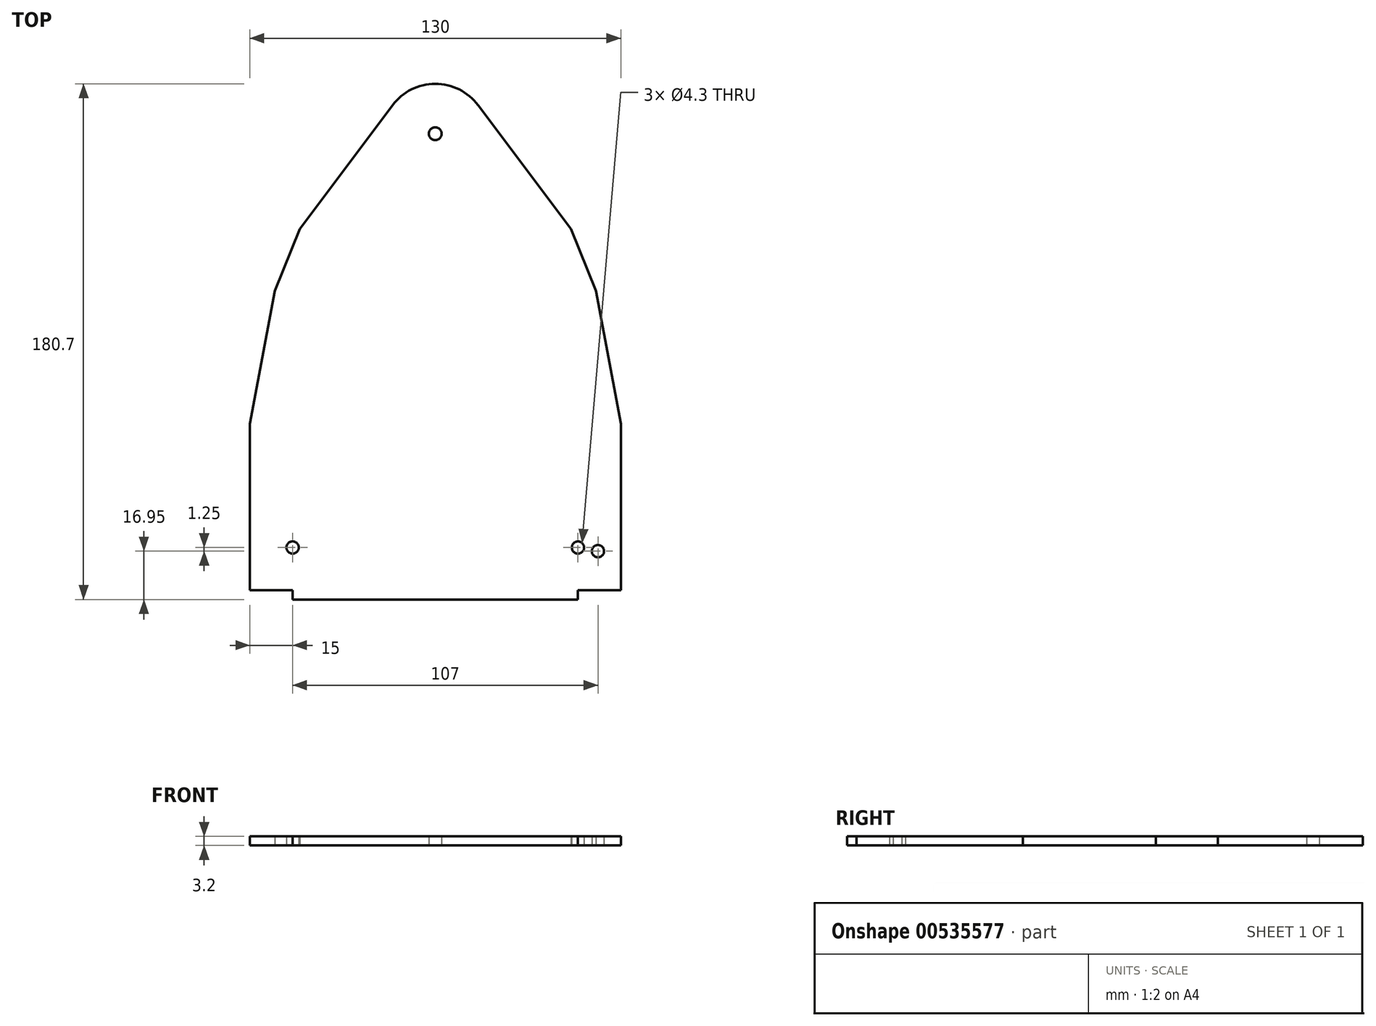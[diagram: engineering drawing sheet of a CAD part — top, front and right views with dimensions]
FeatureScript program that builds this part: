
annotation { "Feature Type Name" : "Feature", "Feature Type Description" : "" }
export const myFeature = defineFeature(function(context is Context, id is Id, definition is map)
    precondition{}
    {
        {
            var Q0;
            Q0=qCreatedBy(makeId("Top.planeOp"),FACE);
            var sketch = newSketch(context, id + "F0", { "sketchPlane" : qUnion([Q0])});
            skLineSegment(sketch, "E0.bottom", {"start": v(65, -75) * mm, "end": v(-65, -75) * mm});
            skLineSegment(sketch, "E0.left", {"start": v(65, -75) * mm, "end": v(65, 75) * mm});
            skPoint(sketch, "E0.middle", {"position": v(0, 0) * mm});
            skLineSegment(sketch, "E1", {"start": v(65, 75) * mm, "end": v(65, 75) * mm});
            skLineSegment(sketch, "E2", {"start": v(65, 75) * mm, "end": v(-65, 75) * mm});
            skLineSegment(sketch, "E3", {"start": v(-65, 75) * mm, "end": v(-65, -75) * mm});
            skLineSegment(sketch, "E4.bottom", {"start": v(-15, 75) * mm, "end": v(15, 75) * mm});
            skLineSegment(sketch, "E4.top", {"start": v(-15, 95) * mm, "end": v(15, 95) * mm});
            skLineSegment(sketch, "E4.left", {"start": v(-15, 75) * mm, "end": v(-15, 95) * mm});
            skLineSegment(sketch, "E4.right", {"start": v(15, 75) * mm, "end": v(15, 95) * mm});
            skPoint(sketch, "E4.middle", {"position": v(0, 85) * mm});
            skCircle(sketch, "E5", {"center": v(0, 85) * mm, "radius": 2.25 * mm});
            skLineSegment(sketch, "E6", {"start": v(-15, 95) * mm, "end": v(-30, 75) * mm});
            skLineSegment(sketch, "E7", {"start": v(-30, 75) * mm, "end": v(-15, 75) * mm});
            skLineSegment(sketch, "E8.MirrorCS", {"start": v(15, 95) * mm, "end": v(30, 75) * mm});
            skLineSegment(sketch, "E9.MirrorCS", {"start": v(30, 75) * mm, "end": v(15, 75) * mm});
            skArc(sketch, "E10", {"start": v(15, 95) * mm, "mid": v(0, 102.5) * mm, "end": v(-15, 95) * mm});
            skSolve(sketch);
        }
        {
            var Q0;
            Q0=qSketchRegion(id+"F0",true);
            extrude(context, id + "F1", {"entities" : qUnion([Q0]), "depth" : 3.2 * mm, "offsetDistance" : 25 * mm});
        }
        {
            var Q0;
            Q0=qCreatedBy(makeId("Top.planeOp"),FACE);
            var sketch = newSketch(context, id + "F2", { "sketchPlane" : qUnion([Q0])});
            skCircle(sketch, "E11", {"center": v(-50, -60) * mm, "radius": 2.15 * mm});
            skCircle(sketch, "E12", {"center": v(50, -60) * mm, "radius": 2.15 * mm});
            skLineSegment(sketch, "E13", {"start": v(-65, 75) * mm, "end": v(-30, 75) * mm});
            skLineSegment(sketch, "E14", {"start": v(-30, 75) * mm, "end": v(-65, 28.33) * mm});
            skLineSegment(sketch, "E15", {"start": v(-65, 28.33) * mm, "end": v(-65, 75) * mm});
            skLineSegment(sketch, "E16", {"start": v(-47.5, 51.67) * mm, "end": v(-20.95, 87.07) * mm});
            skLineSegment(sketch, "E17", {"start": v(-47.5, 51.67) * mm, "end": v(-65, 8.33) * mm});
            skLineSegment(sketch, "E18", {"start": v(-65, 8.33) * mm, "end": v(-65, 28.33) * mm});
            skLineSegment(sketch, "E19", {"start": v(-56.25, 30) * mm, "end": v(-65, -16.67) * mm});
            skLineSegment(sketch, "E20", {"start": v(-65, -16.67) * mm, "end": v(-65, 8.33) * mm});
            skLineSegment(sketch, "E21", {"start": v(-65, 75) * mm, "end": v(-65, -16.67) * mm});
            skLineSegment(sketch, "E22.MirrorCS", {"start": v(65, 75) * mm, "end": v(65, -16.67) * mm});
            skLineSegment(sketch, "E23.MirrorCS", {"start": v(56.25, 30) * mm, "end": v(65, -16.67) * mm});
            skLineSegment(sketch, "E24.MirrorCS", {"start": v(47.5, 51.67) * mm, "end": v(65, 8.33) * mm});
            skLineSegment(sketch, "E25.MirrorCS", {"start": v(47.5, 51.67) * mm, "end": v(20.95, 87.07) * mm});
            skLineSegment(sketch, "E26.MirrorCS", {"start": v(65, 75) * mm, "end": v(30, 75) * mm});
            skCircle(sketch, "E27", {"center": v(57, -61.25) * mm, "radius": 2.15 * mm});
            skSolve(sketch);
        }
        {
            var Q0;
            Q0=qSketchRegion(id+"F2",true);
            extrude(context, id + "F3", {"entities" : qUnion([Q0]), "operationType" : NewBodyOperationType.REMOVE, "depth" : 54 * mm, "offsetDistance" : 25 * mm});
        }
        {
            var Q0;
            Q0=qCreatedBy(makeId("Top.planeOp"),FACE);
            var sketch = newSketch(context, id + "F4", { "sketchPlane" : qUnion([Q0])});
            skLineSegment(sketch, "E28.bottom", {"start": v(-50, -75) * mm, "end": v(50, -75) * mm});
            skLineSegment(sketch, "E28.top", {"start": v(-50, -78.2) * mm, "end": v(50, -78.2) * mm});
            skLineSegment(sketch, "E28.left", {"start": v(-50, -75) * mm, "end": v(-50, -78.2) * mm});
            skLineSegment(sketch, "E28.right", {"start": v(50, -75) * mm, "end": v(50, -78.2) * mm});
            skPoint(sketch, "E28.middle", {"position": v(0, -76.6) * mm});
            skSolve(sketch);
        }
        {
            var Q0;
            Q0 = qSketchRegion(id + "F4", true);
            extrude(context, id + "F5", {"entities" : qUnion([Q0]), "operationType" : NewBodyOperationType.ADD, "depth" : 3.2 * mm, "offsetDistance" : 25 * mm});
        }
    });
